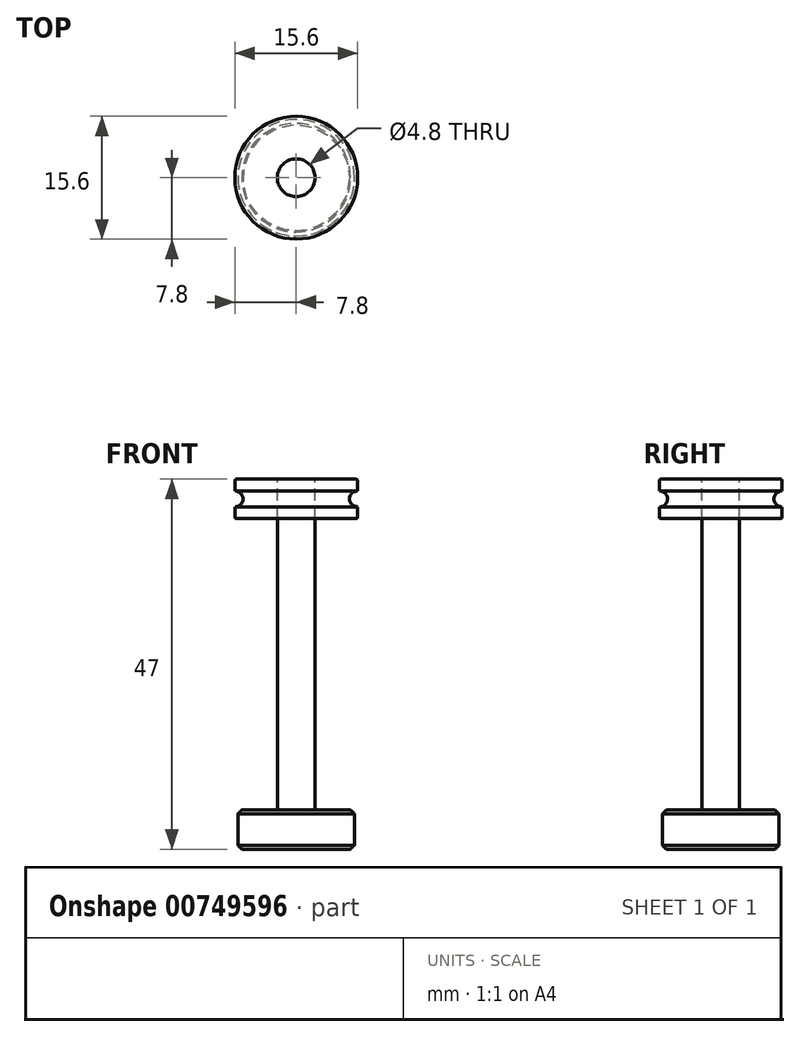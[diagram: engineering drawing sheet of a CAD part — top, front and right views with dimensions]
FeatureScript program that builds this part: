
annotation { "Feature Type Name" : "Feature", "Feature Type Description" : "" }
export const myFeature = defineFeature(function(context is Context, id is Id, definition is map)
    precondition{}
    {
        {
            var Q0;
            Q0=qCreatedBy(makeId("Front.planeOp"),FACE);
            var sketch = newSketch(context, id + "F0", { "sketchPlane" : qUnion([Q0])});
            skLineSegment(sketch, "E0", {"start": v(0, 0) * mm, "end": v(-7.4, 0) * mm});
            skLineSegment(sketch, "E1", {"start": v(-7.4, 0) * mm, "end": v(-7.4, 5) * mm});
            skLineSegment(sketch, "E2", {"start": v(-7.4, 5) * mm, "end": v(-2.4, 5) * mm});
            skLineSegment(sketch, "E3", {"start": v(-2.4, 5) * mm, "end": v(-2.4, 47) * mm});
            skLineSegment(sketch, "E4", {"start": v(-2.4, 47) * mm, "end": v(0, 47) * mm});
            skLineSegment(sketch, "E5", {"start": v(0, 47) * mm, "end": v(0, 0) * mm});
            skLineSegment(sketch, "E6.bottom", {"start": v(-2.4, 47) * mm, "end": v(-7.8, 47) * mm});
            skLineSegment(sketch, "E6.top", {"start": v(-2.4, 42) * mm, "end": v(-7.8, 42) * mm});
            skLineSegment(sketch, "E6.left", {"start": v(-2.4, 47) * mm, "end": v(-2.4, 42) * mm});
            skLineSegment(sketch, "E6.right", {"start": v(-7.8, 47) * mm, "end": v(-7.8, 42) * mm});
            skArc(sketch, "E7", {"start": v(-7.8, 43.5) * mm, "mid": v(-6.75, 44.5) * mm, "end": v(-7.8, 45.5) * mm});
            skSolve(sketch);
        }
        {
            var Q0;
            Q0=makeQuery(id+"F0.imprint","IMPRINT",FACE,{"disambiguationData":[TD([[makeQuery(id+"F0.imprint","IMPRINT",EDGE,{"derivedFrom":sQuery(id+"F0.wireOp",EDGE,"E0")}),-1.0]])]});
            var Q1;
            Q1=sQuery(id+"F0.wireOp",EDGE,"E5");
            revolve(context, id + "F1", {"surfaceOperationType" : NewSurfaceOperationType.NEW, "entities" : qUnion([Q0]), "axis" : qUnion([Q1]), "revolveType" : RevolveType.FULL});
        }
        {
            var Q0;
            Q0=makeQuery(id+"F1.opRevolve","SWEPT_EDGE",EDGE,{"disambiguationData":[OSD([sQuery(id+"F0.wireOp",EDGE,"E1"),sQuery(id+"F0.wireOp",EDGE,"E2")])]});
            var Q1;
            Q1=makeQuery(id+"F1.opRevolve","SWEPT_EDGE",EDGE,{"disambiguationData":[OSD([sQuery(id+"F0.wireOp",EDGE,"E0"),sQuery(id+"F0.wireOp",EDGE,"E1")])]});
            chamfer(context, id + "F2", {"entities" : qUnion([Q0, Q1]), "width" : 0.5 * mm, "tangentPropagation" : true});
        }
        {
            var Q0;
            Q0=makeQuery(id+"F0.imprint","IMPRINT",FACE,{"disambiguationData":[TD([[makeQuery(id+"F0.imprint","IMPRINT",EDGE,{"derivedFrom":sQuery(id+"F0.wireOp",EDGE,"E6.bottom")}),1.0]])]});
            var Q1;
            Q1=sQuery(id+"F0.wireOp",EDGE,"E5");
            revolve(context, id + "F3", {"surfaceOperationType" : NewSurfaceOperationType.NEW, "entities" : qUnion([Q0]), "axis" : qUnion([Q1]), "revolveType" : RevolveType.FULL});
        }
        {
            var Q0;
            Q0=makeQuery(id+"F3.opRevolve","SWEPT_EDGE",EDGE,{"disambiguationData":[OSD([sQuery(id+"F0.wireOp",EDGE,"E6.bottom"),sQuery(id+"F0.wireOp",EDGE,"E6.right")])]});
            var Q1;
            Q1=makeQuery(id+"F3.opRevolve","SWEPT_EDGE",EDGE,{"disambiguationData":[OSD([sQuery(id+"F0.wireOp",EDGE,"E6.top"),sQuery(id+"F0.wireOp",EDGE,"E6.right")])]});
            fillet(context, id + "F4", {"entities" : qUnion([Q0, Q1]), "radius" : 0.2 * mm, "tangentPropagation" : true, "allowEdgeOverflow" : false});
        }
    });
